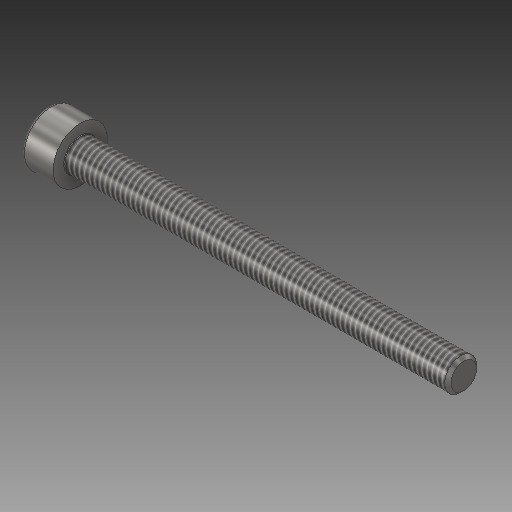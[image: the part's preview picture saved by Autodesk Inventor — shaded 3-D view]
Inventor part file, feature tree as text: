
AUTODESK INVENTOR PART (.ipt)
format: ipt  version: 2018 (Build 220112000, 112)  size: 195,584 bytes
history: native  units: mm
features: other x6, sketch x2, plane x1
ambient origin geometry x8: Origin, YZ Plane, XZ Plane, XY Plane, X Axis, Y Axis, Z Axis, Center Point
bodies: Solid1 (feature_tree)
feature tree (9):
  other  "ANSI B18.3.1M - M5x0.8 x 60NEW_MIR.ipt"
  other  "Solid1::ANSI B18.3.1M - M5x0.8 x 60NEW_MIR.ipt"
  other  "TaggingFeature1"
  sketch  "Sketch1"  dims[d0=10.0mm]
  sketch  "Sketch2"  dims[d19=0.0mm d28=0.0mm d29=0.0mm]
  plane  "Work Plane1"
  other  "Align 2D"
  other  "Align1"
  other  "Insert In1"
